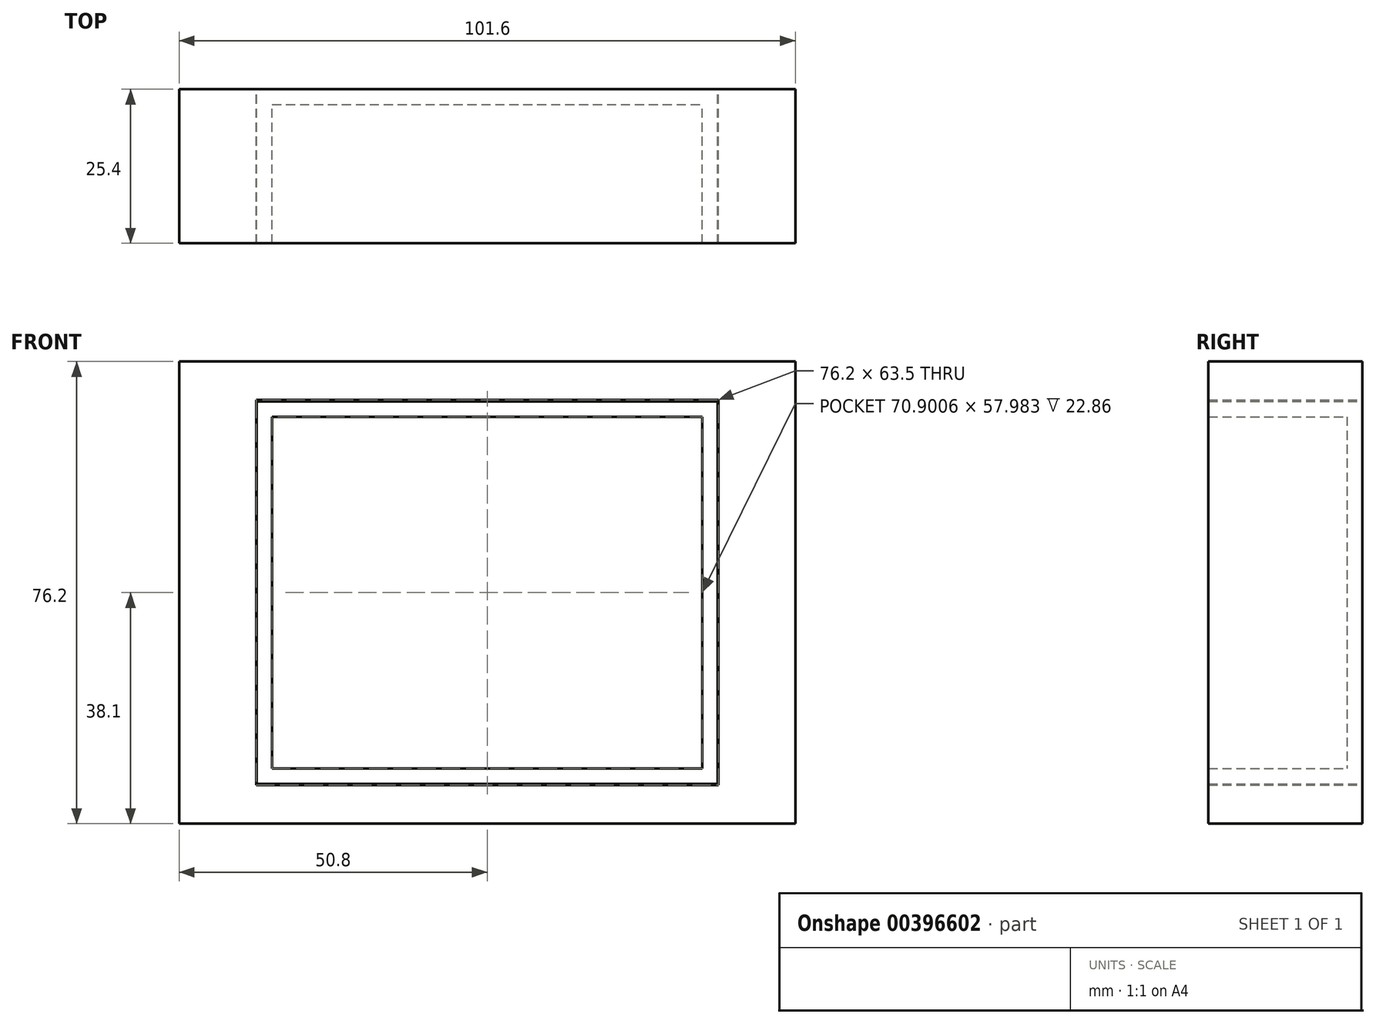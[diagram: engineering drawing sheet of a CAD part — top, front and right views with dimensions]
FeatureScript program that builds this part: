
annotation { "Feature Type Name" : "Feature", "Feature Type Description" : "" }
export const myFeature = defineFeature(function(context is Context, id is Id, definition is map)
    precondition{}
    {
        {
            var Q0;
            Q0=qCreatedBy(makeId("Front.planeOp"),FACE);
            var sketch = newSketch(context, id + "F0", { "sketchPlane" : qUnion([Q0])});
            skLineSegment(sketch, "E0.bottom", {"start": v(-38.1, -31.75) * mm, "end": v(38.1, -31.75) * mm});
            skLineSegment(sketch, "E0.top", {"start": v(-38.1, 31.75) * mm, "end": v(38.1, 31.75) * mm});
            skLineSegment(sketch, "E0.left", {"start": v(-38.1, -31.75) * mm, "end": v(-38.1, 31.75) * mm});
            skLineSegment(sketch, "E0.right", {"start": v(38.1, -31.75) * mm, "end": v(38.1, 31.75) * mm});
            skPoint(sketch, "E0.middle", {"position": v(0, 0) * mm});
            skLineSegment(sketch, "E1.bottom", {"start": v(-50.8, -38.1) * mm, "end": v(50.8, -38.1) * mm});
            skLineSegment(sketch, "E1.top", {"start": v(-50.8, 38.1) * mm, "end": v(50.8, 38.1) * mm});
            skLineSegment(sketch, "E1.left", {"start": v(-50.8, -38.1) * mm, "end": v(-50.8, 38.1) * mm});
            skLineSegment(sketch, "E1.right", {"start": v(50.8, -38.1) * mm, "end": v(50.8, 38.1) * mm});
            skSolve(sketch);
        }
        {
            var Q0;
            Q0 = qSketchRegion(id + "F0", true);
            extrude(context, id + "F1", {"entities" : qUnion([Q0]), "depth" : 25.4 * mm});
        }
        {
            var Q0;
            Q0=qCreatedBy(makeId("Front.planeOp"),FACE);
            var sketch = newSketch(context, id + "F2", { "sketchPlane" : qUnion([Q0])});
            skLineSegment(sketch, "E2.bottom", {"start": v(-38, 31.53) * mm, "end": v(38, 31.53) * mm});
            skLineSegment(sketch, "E2.top", {"start": v(-38, -31.53) * mm, "end": v(38, -31.53) * mm});
            skLineSegment(sketch, "E2.left", {"start": v(-38, 31.53) * mm, "end": v(-38, -31.53) * mm});
            skLineSegment(sketch, "E2.right", {"start": v(38, 31.53) * mm, "end": v(38, -31.53) * mm});
            skPoint(sketch, "E2.middle", {"position": v(0, 0) * mm});
            skSolve(sketch);
        }
        {
            var Q0;
            Q0 = qSketchRegion(id + "F2", true);
            extrude(context, id + "F3", {"entities" : qUnion([Q0]), "depth" : 25.4 * mm});
        }
        {
            var Q0;
            Q0=makeQuery(id+"F3.opExtrude","CAP_FACE",FACE,{"disambiguationData":[OSD([sQuery(id+"F2.wireOp",EDGE,"E2.bottom"),sQuery(id+"F2.wireOp",EDGE,"E2.top"),sQuery(id+"F2.wireOp",EDGE,"E2.left"),sQuery(id+"F2.wireOp",EDGE,"E2.right")])],"isStart":false});
            shell(context, id + "F4", {"entities" : qUnion([Q0]), "thickness" : 2.54 * mm});
        }
    });
